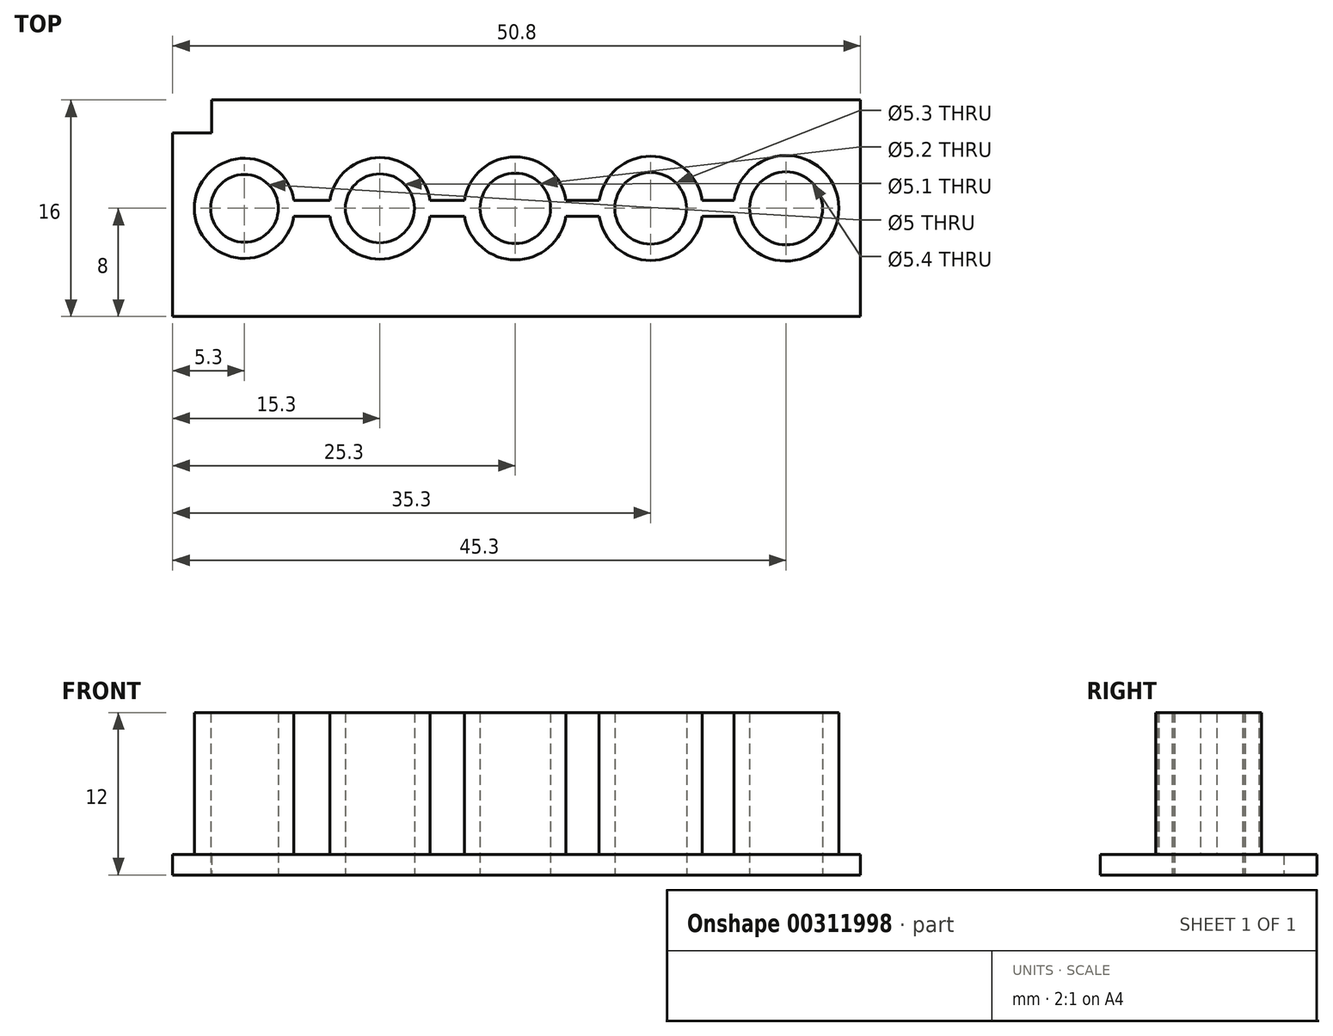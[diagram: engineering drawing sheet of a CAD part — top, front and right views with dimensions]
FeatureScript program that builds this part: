
annotation { "Feature Type Name" : "Feature", "Feature Type Description" : "" }
export const myFeature = defineFeature(function(context is Context, id is Id, definition is map)
    precondition{}
    {
        {
            var Q0;
            Q0=qCreatedBy(makeId("Top.planeOp"),FACE);
            var sketch = newSketch(context, id + "F0", { "sketchPlane" : qUnion([Q0])});
            skLineSegment(sketch, "E0.top", {"start": v(-25.3, -8) * mm, "end": v(25.5, -8) * mm});
            skPoint(sketch, "E0.middle", {"position": v(0, 0) * mm});
            skCircle(sketch, "E1", {"center": v(-20, 0) * mm, "radius": 2.5 * mm});
            skCircle(sketch, "E2", {"center": v(-20, 0) * mm, "radius": 3.7 * mm});
            skPoint(sketch, "E3", {"position": v(-10, 0) * mm});
            skCircle(sketch, "E4", {"center": v(-10, 0) * mm, "radius": 2.55 * mm});
            skCircle(sketch, "E5", {"center": v(-10, 0) * mm, "radius": 3.75 * mm});
            skPoint(sketch, "E6", {"position": v(10, 0) * mm});
            skCircle(sketch, "E7", {"center": v(0, 0) * mm, "radius": 2.6 * mm});
            skCircle(sketch, "E8", {"center": v(0, 0) * mm, "radius": 3.8 * mm});
            skCircle(sketch, "E9", {"center": v(10, 0) * mm, "radius": 2.65 * mm});
            skCircle(sketch, "E10", {"center": v(10, 0) * mm, "radius": 3.85 * mm});
            skCircle(sketch, "E11", {"center": v(20, 0) * mm, "radius": 2.7 * mm});
            skCircle(sketch, "E12", {"center": v(20, 0) * mm, "radius": 3.9 * mm});
            skPoint(sketch, "E13.orphan", {"position": v(-25.3, 8) * mm});
            skLineSegment(sketch, "E14", {"start": v(-16.35, 0.6) * mm, "end": v(-13.7, 0.6) * mm});
            skLineSegment(sketch, "E15", {"start": v(-16.35, -0.6) * mm, "end": v(-13.7, -0.6) * mm});
            skLineSegment(sketch, "E16", {"start": v(-25.3, -8) * mm, "end": v(-25.3, 8) * mm});
            skLineSegment(sketch, "E17", {"start": v(-25.3, 0) * mm, "end": v(-23.7, 0) * mm, "construction": true});
            skLineSegment(sketch, "E18", {"start": v(25.5, -8) * mm, "end": v(25.5, 8) * mm});
            skLineSegment(sketch, "E19", {"start": v(25.5, 8) * mm, "end": v(-25.3, 8) * mm});
            skLineSegment(sketch, "E20", {"start": v(-6.3, 0.6) * mm, "end": v(-3.75, 0.6) * mm});
            skLineSegment(sketch, "E21", {"start": v(-6.3, -0.6) * mm, "end": v(-3.75, -0.6) * mm});
            skLineSegment(sketch, "E22", {"start": v(3.75, 0.6) * mm, "end": v(6.2, 0.6) * mm});
            skLineSegment(sketch, "E23", {"start": v(3.75, -0.6) * mm, "end": v(6.2, -0.6) * mm});
            skLineSegment(sketch, "E24", {"start": v(13.8, 0.6) * mm, "end": v(16.15, 0.6) * mm});
            skLineSegment(sketch, "E25", {"start": v(13.8, -0.6) * mm, "end": v(16.15, -0.6) * mm});
            skPoint(sketch, "E25.startSnap0", {"position": v(4.97, -0.6) * mm});
            skLineSegment(sketch, "E26.bottom", {"start": v(-22.42, 8) * mm, "end": v(-25.3, 8) * mm});
            skLineSegment(sketch, "E26.top", {"start": v(-22.42, 5.55) * mm, "end": v(-25.3, 5.55) * mm});
            skLineSegment(sketch, "E26.left", {"start": v(-22.42, 8) * mm, "end": v(-22.42, 5.55) * mm});
            skLineSegment(sketch, "E26.right", {"start": v(-25.3, 8) * mm, "end": v(-25.3, 5.55) * mm});
            skSolve(sketch);
        }
        {
            var Q0;
            Q0=makeQuery(id+"F0.imprint","IMPRINT",FACE,{"disambiguationData":[TD([[makeQuery(id+"F0.imprint","IMPRINT",EDGE,{"derivedFrom":sQuery(id+"F0.wireOp",EDGE,"E0.top")}),1.0]])]});
            extrude(context, id + "F1", {"entities" : qUnion([Q0]), "depth" : 1.5 * mm});
        }
        {
            var Q0;
            Q0=makeQuery(id+"F0.imprint","IMPRINT",FACE,{"disambiguationData":[TD([[makeQuery(id+"F0.imprint","IMPRINT",EDGE,{"derivedFrom":sQuery(id+"F0.wireOp",EDGE,"E1")}),-1.0]])]});
            var Q1;
            {var subQ0=sQuery(id+"F0.wireOp",EDGE,"E5");var subQ1=sQuery(id+"F0.wireOp",EDGE,"k0xYYLFm-EbhM-nypB-a5wA-Y3ieiyBQ3hta");var subQ2=makeQuery(id+"F0.imprint","INTERSECT",VERTEX,{"disambiguationData":[OD(0.0)],"derivedFrom":[subQ1,subQ0]});Q1=makeQuery(id+"F0.imprint","IMPRINT",FACE,{"disambiguationData":[TD([[makeQuery(id+"F0.imprint","IMPRINT",EDGE,{"disambiguationData":[TD([[subQ2,-1.0]])],"derivedFrom":subQ1}),-1.0]])]});}
            var Q2;
            {var subQ0=sQuery(id+"F0.wireOp",EDGE,"E5");var subQ1=sQuery(id+"F0.wireOp",EDGE,"k0xYYLFm-EbhM-nypB-a5wA-Y3ieiyBQ3hta");var subQ2=makeQuery(id+"F0.imprint","INTERSECT",VERTEX,{"disambiguationData":[OD(0.0)],"derivedFrom":[subQ1,subQ0]});Q2=makeQuery(id+"F0.imprint","IMPRINT",FACE,{"disambiguationData":[TD([[makeQuery(id+"F0.imprint","IMPRINT",EDGE,{"disambiguationData":[TD([[subQ2,-1.0]])],"derivedFrom":subQ1}),1.0]])]});}
            var Q3;
            {var subQ0=sQuery(id+"F0.wireOp",EDGE,"E8");var subQ1=sQuery(id+"F0.wireOp",EDGE,"k0xYYLFm-EbhM-nypB-a5wA-Y3ieiyBQ3hta");var subQ2=makeQuery(id+"F0.imprint","INTERSECT",VERTEX,{"derivedFrom":[subQ1,subQ0]});Q3=makeQuery(id+"F0.imprint","IMPRINT",FACE,{"disambiguationData":[TD([[makeQuery(id+"F0.imprint","IMPRINT",EDGE,{"disambiguationData":[TD([[subQ2,1.0]])],"derivedFrom":subQ1}),-1.0]])]});}
            var Q4;
            {var subQ0=sQuery(id+"F0.wireOp",EDGE,"E8");var subQ1=sQuery(id+"F0.wireOp",EDGE,"k0xYYLFm-EbhM-nypB-a5wA-Y3ieiyBQ3hta");var subQ2=makeQuery(id+"F0.imprint","INTERSECT",VERTEX,{"derivedFrom":[subQ1,subQ0]});Q4=makeQuery(id+"F0.imprint","IMPRINT",FACE,{"disambiguationData":[TD([[makeQuery(id+"F0.imprint","IMPRINT",EDGE,{"disambiguationData":[TD([[subQ2,1.0]])],"derivedFrom":subQ1}),1.0]])]});}
            var Q5;
            {var subQ0=sQuery(id+"F0.wireOp",EDGE,"E10");var subQ1=sQuery(id+"F0.wireOp",EDGE,"O8aI1fMW-w7MF-1uQT-BdUp-VbcJrZ8hB7Jf");var subQ2=makeQuery(id+"F0.imprint","INTERSECT",VERTEX,{"disambiguationData":[OD(0.0)],"derivedFrom":[subQ1,subQ0]});Q5=makeQuery(id+"F0.imprint","IMPRINT",FACE,{"disambiguationData":[TD([[makeQuery(id+"F0.imprint","IMPRINT",EDGE,{"disambiguationData":[TD([[subQ2,-1.0]])],"derivedFrom":subQ1}),-1.0]])]});}
            var Q6;
            {var subQ0=sQuery(id+"F0.wireOp",EDGE,"E10");var subQ1=sQuery(id+"F0.wireOp",EDGE,"O8aI1fMW-w7MF-1uQT-BdUp-VbcJrZ8hB7Jf");var subQ2=makeQuery(id+"F0.imprint","INTERSECT",VERTEX,{"disambiguationData":[OD(0.0)],"derivedFrom":[subQ1,subQ0]});Q6=makeQuery(id+"F0.imprint","IMPRINT",FACE,{"disambiguationData":[TD([[makeQuery(id+"F0.imprint","IMPRINT",EDGE,{"disambiguationData":[TD([[subQ2,-1.0]])],"derivedFrom":subQ1}),1.0]])]});}
            var Q7;
            {var subQ0=sQuery(id+"F0.wireOp",EDGE,"E12");var subQ1=sQuery(id+"F0.wireOp",EDGE,"dwUy30dI-npy4-pwrf-FtxV-8h1p0pJB7vt0");var subQ2=makeQuery(id+"F0.imprint","INTERSECT",VERTEX,{"derivedFrom":[subQ1,subQ0]});Q7=makeQuery(id+"F0.imprint","IMPRINT",FACE,{"disambiguationData":[TD([[makeQuery(id+"F0.imprint","IMPRINT",EDGE,{"disambiguationData":[TD([[subQ2,1.0]])],"derivedFrom":subQ1}),1.0]])]});}
            var Q8;
            {var subQ0=sQuery(id+"F0.wireOp",EDGE,"E12");var subQ1=sQuery(id+"F0.wireOp",EDGE,"dwUy30dI-npy4-pwrf-FtxV-8h1p0pJB7vt0");var subQ2=makeQuery(id+"F0.imprint","INTERSECT",VERTEX,{"derivedFrom":[subQ1,subQ0]});Q8=makeQuery(id+"F0.imprint","IMPRINT",FACE,{"disambiguationData":[TD([[makeQuery(id+"F0.imprint","IMPRINT",EDGE,{"disambiguationData":[TD([[subQ2,1.0]])],"derivedFrom":subQ1}),-1.0]])]});}
            var Q9;
            {var subQ0=sQuery(id+"F0.wireOp",EDGE,"E14");Q9=makeQuery(id+"F0.imprint","IMPRINT",FACE,{"disambiguationData":[TD([[makeQuery(id+"F0.imprint","IMPRINT",EDGE,{"derivedFrom":subQ0}),-1.0]])]});}
            var Q10;
            Q10=makeQuery(id+"F0.imprint","IMPRINT",FACE,{"disambiguationData":[TD([[makeQuery(id+"F0.imprint","IMPRINT",EDGE,{"derivedFrom":sQuery(id+"F0.wireOp",EDGE,"E4")}),-1.0]])]});
            var Q11;
            {var subQ0=sQuery(id+"F0.wireOp",EDGE,"E20");Q11=makeQuery(id+"F0.imprint","IMPRINT",FACE,{"disambiguationData":[TD([[makeQuery(id+"F0.imprint","IMPRINT",EDGE,{"derivedFrom":subQ0}),-1.0]])]});}
            var Q12;
            Q12=makeQuery(id+"F0.imprint","IMPRINT",FACE,{"disambiguationData":[TD([[makeQuery(id+"F0.imprint","IMPRINT",EDGE,{"derivedFrom":sQuery(id+"F0.wireOp",EDGE,"E7")}),-1.0]])]});
            var Q13;
            {var subQ0=sQuery(id+"F0.wireOp",EDGE,"E22");Q13=makeQuery(id+"F0.imprint","IMPRINT",FACE,{"disambiguationData":[TD([[makeQuery(id+"F0.imprint","IMPRINT",EDGE,{"derivedFrom":subQ0}),-1.0]])]});}
            var Q14;
            Q14=makeQuery(id+"F0.imprint","IMPRINT",FACE,{"disambiguationData":[TD([[makeQuery(id+"F0.imprint","IMPRINT",EDGE,{"derivedFrom":sQuery(id+"F0.wireOp",EDGE,"E9")}),-1.0]])]});
            var Q15;
            {var subQ0=sQuery(id+"F0.wireOp",EDGE,"E24");Q15=makeQuery(id+"F0.imprint","IMPRINT",FACE,{"disambiguationData":[TD([[makeQuery(id+"F0.imprint","IMPRINT",EDGE,{"derivedFrom":subQ0}),-1.0]])]});}
            var Q16;
            Q16=makeQuery(id+"F0.imprint","IMPRINT",FACE,{"disambiguationData":[TD([[makeQuery(id+"F0.imprint","IMPRINT",EDGE,{"derivedFrom":sQuery(id+"F0.wireOp",EDGE,"E11")}),-1.0]])]});
            extrude(context, id + "F2", {"entities" : qUnion([Q0, Q1, Q2, Q3, Q4, Q5, Q6, Q7, Q8, Q9, Q10, Q11, Q12, Q13, Q14, Q15, Q16]), "operationType" : NewBodyOperationType.ADD, "depth" : 12 * mm});
        }
    });
